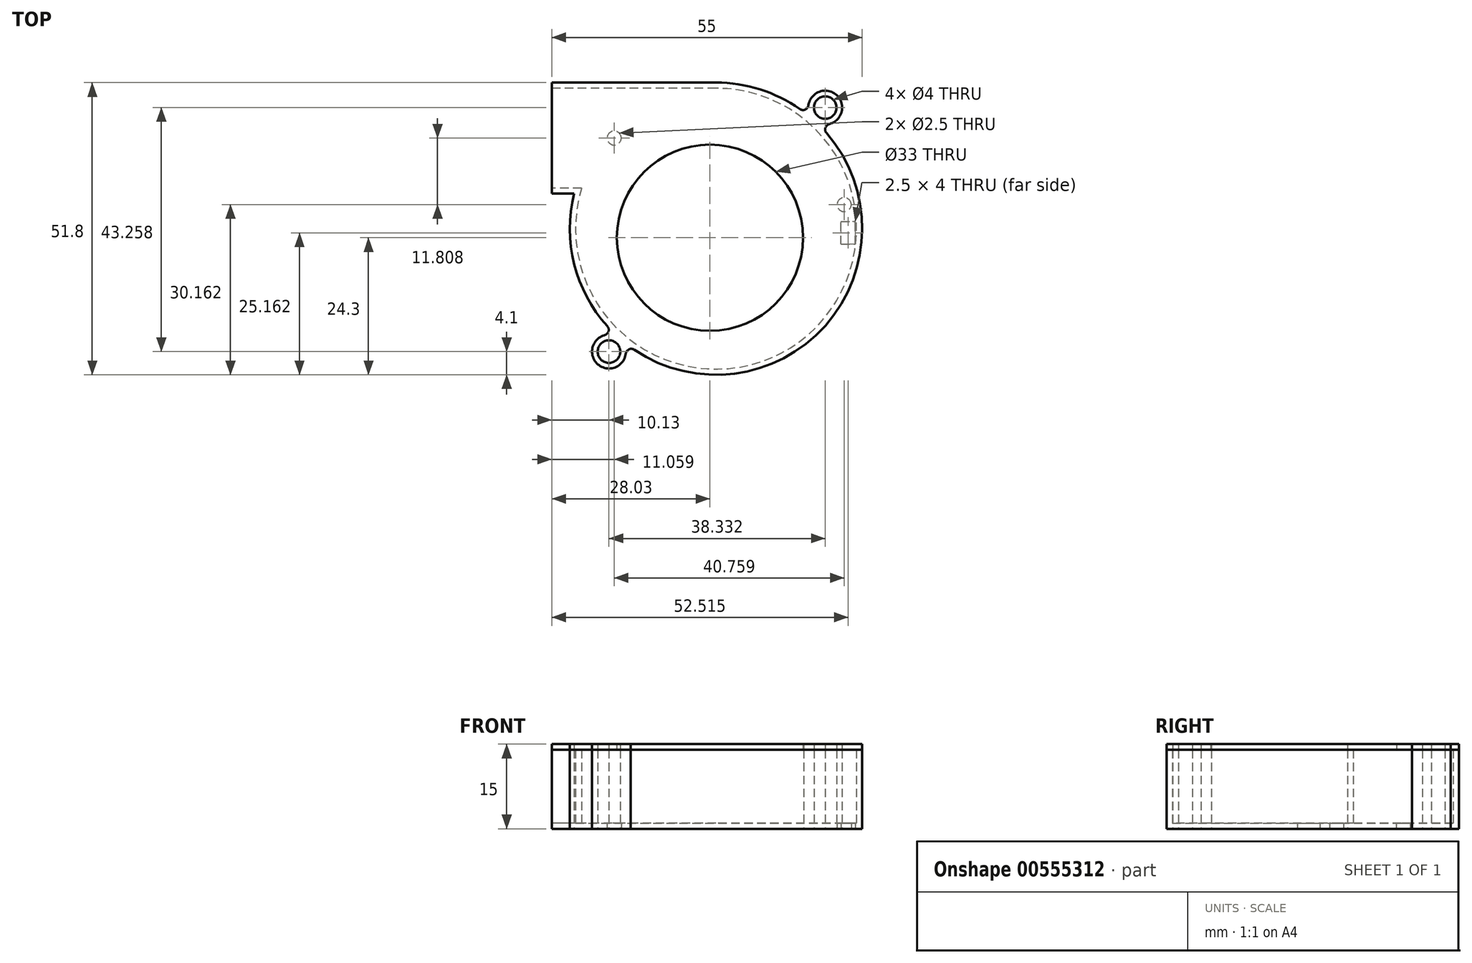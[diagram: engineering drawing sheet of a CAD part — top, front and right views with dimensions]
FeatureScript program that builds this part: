
annotation { "Feature Type Name" : "Feature", "Feature Type Description" : "" }
export const myFeature = defineFeature(function(context is Context, id is Id, definition is map)
    precondition{}
    {
        {
            var Q0;
            Q0=qCreatedBy(makeId("Top.planeOp"),FACE);
            var sketch = newSketch(context, id + "F0", { "sketchPlane" : qUnion([Q0])});
            skCircle(sketch, "E0", {"center": v(0, 0) * mm, "radius": 16.5 * mm});
            skCircle(sketch, "E1", {"center": v(1.07, 1.6) * mm, "radius": 25.9 * mm});
            skLineSegment(sketch, "E2.bottom", {"start": v(26.97, 27.5) * mm, "end": v(-24.83, 27.5) * mm, "construction": true});
            skLineSegment(sketch, "E2.top", {"start": v(26.97, -24.3) * mm, "end": v(-24.83, -24.3) * mm, "construction": true});
            skLineSegment(sketch, "E2.left", {"start": v(26.97, 27.5) * mm, "end": v(26.97, -24.3) * mm, "construction": true});
            skLineSegment(sketch, "E2.right", {"start": v(-24.83, 27.5) * mm, "end": v(-24.83, -24.3) * mm, "construction": true});
            skLineSegment(sketch, "E3", {"start": v(1.07, 27.5) * mm, "end": v(-28.03, 27.5) * mm});
            skPoint(sketch, "E3.startSnap0", {"position": v(1.07, 27.5) * mm});
            skLineSegment(sketch, "E4", {"start": v(-28.03, 27.5) * mm, "end": v(-28.03, 7.8) * mm});
            skLineSegment(sketch, "E5", {"start": v(-28.03, 7.8) * mm, "end": v(-24.07, 7.8) * mm});
            skCircle(sketch, "E6", {"center": v(20.43, 23.06) * mm, "radius": 2 * mm});
            skCircle(sketch, "E7", {"center": v(-17.9, -20.2) * mm, "radius": 2 * mm});
            skLineSegment(sketch, "E8", {"start": v(-17.9, -20.2) * mm, "end": v(24.43, 27.57) * mm, "construction": true});
            skCircle(sketch, "E9", {"center": v(20.43, 23.06) * mm, "radius": 3 * mm});
            skCircle(sketch, "E10", {"center": v(-17.9, -20.2) * mm, "radius": 3 * mm});
            skCircle(sketch, "E11", {"center": v(0, 0) * mm, "radius": 24.5 * mm, "construction": true});
            skCircle(sketch, "E12", {"center": v(-16.97, 17.67) * mm, "radius": 1.25 * mm});
            skCircle(sketch, "E13.1.0", {"center": v(23.79, 5.86) * mm, "radius": 1.25 * mm});
            skLineSegment(sketch, "E13.anchor1", {"start": v(0, 0) * mm, "end": v(-16.97, 17.67) * mm, "construction": true});
            skLineSegment(sketch, "E13.anchor2", {"start": v(0, 0) * mm, "end": v(23.79, 5.86) * mm, "construction": true});
            skLineSegment(sketch, "E14.bottom", {"start": v(23.23, -1.14) * mm, "end": v(25.73, -1.14) * mm});
            skLineSegment(sketch, "E14.top", {"start": v(23.23, 2.86) * mm, "end": v(25.73, 2.86) * mm});
            skLineSegment(sketch, "E14.left", {"start": v(23.23, -1.14) * mm, "end": v(23.23, 2.86) * mm});
            skLineSegment(sketch, "E14.right", {"start": v(25.73, -1.14) * mm, "end": v(25.73, 2.86) * mm});
            skPoint(sketch, "E14.middle", {"position": v(24.48, 0.86) * mm});
            skLineSegment(sketch, "E15", {"start": v(-15.28, -18.75) * mm, "end": v(-15.14, -18.6) * mm});
            skLineSegment(sketch, "E16", {"start": v(-16.65, -17.28) * mm, "end": v(-16.77, -17.42) * mm});
            skLineSegment(sketch, "E17", {"start": v(17.8, 21.6) * mm, "end": v(17.69, 21.47) * mm});
            skLineSegment(sketch, "E18", {"start": v(19.3, 20.28) * mm, "end": v(19.17, 20.13) * mm});
            skLineSegment(sketch, "E19", {"start": v(-28.03, 26.5) * mm, "end": v(1.07, 26.5) * mm});
            skLineSegment(sketch, "E20", {"start": v(-28.03, 8.8) * mm, "end": v(-22.76, 8.8) * mm});
            skArc(sketch, "E21", {"start": v(-22.76, 8.8) * mm, "mid": v(15.92, -18.4) * mm, "end": v(1.07, 26.5) * mm});
            skSolve(sketch);
        }
        {
            var Q0;
            {var subQ0=sQuery(id+"F0.wireOp",EDGE,"E3");Q0=makeQuery(id+"F0.imprint","IMPRINT",FACE,{"disambiguationData":[TD([[makeQuery(id+"F0.imprint","IMPRINT",EDGE,{"derivedFrom":subQ0}),1.0]])]});}
            var Q1;
            Q1=makeQuery(id+"F0.imprint","IMPRINT",FACE,{"disambiguationData":[TD([[makeQuery(id+"F0.imprint","IMPRINT",EDGE,{"derivedFrom":sQuery(id+"F0.wireOp",EDGE,"E0")}),-1.0]])]});
            var Q2;
            Q2=makeQuery(id+"F0.imprint","IMPRINT",FACE,{"disambiguationData":[TD([[makeQuery(id+"F0.imprint","IMPRINT",EDGE,{"derivedFrom":sQuery(id+"F0.wireOp",EDGE,"E0")}),1.0]])]});
            var Q3;
            Q3=makeQuery(id+"F0.imprint","IMPRINT",FACE,{"disambiguationData":[TD([[makeQuery(id+"F0.imprint","IMPRINT",EDGE,{"derivedFrom":sQuery(id+"F0.wireOp",EDGE,"E7")}),-1.0]])]});
            var Q4;
            Q4=makeQuery(id+"F0.imprint","IMPRINT",FACE,{"disambiguationData":[TD([[makeQuery(id+"F0.imprint","IMPRINT",EDGE,{"derivedFrom":sQuery(id+"F0.wireOp",EDGE,"E6")}),-1.0]])]});
            var Q5;
            {var subQ0=sQuery(id+"F0.wireOp",EDGE,"E18");Q5=makeQuery(id+"F0.imprint","IMPRINT",FACE,{"disambiguationData":[TD([[makeQuery(id+"F0.imprint","IMPRINT",EDGE,{"derivedFrom":subQ0}),-1.0]])]});}
            var Q6;
            {var subQ0=sQuery(id+"F0.wireOp",EDGE,"E17");Q6=makeQuery(id+"F0.imprint","IMPRINT",FACE,{"disambiguationData":[TD([[makeQuery(id+"F0.imprint","IMPRINT",EDGE,{"derivedFrom":subQ0}),1.0]])]});}
            var Q7;
            {var subQ0=sQuery(id+"F0.wireOp",EDGE,"E15");Q7=makeQuery(id+"F0.imprint","IMPRINT",FACE,{"disambiguationData":[TD([[makeQuery(id+"F0.imprint","IMPRINT",EDGE,{"derivedFrom":subQ0}),1.0]])]});}
            var Q8;
            {var subQ0=sQuery(id+"F0.wireOp",EDGE,"E16");Q8=makeQuery(id+"F0.imprint","IMPRINT",FACE,{"disambiguationData":[TD([[makeQuery(id+"F0.imprint","IMPRINT",EDGE,{"derivedFrom":subQ0}),1.0]])]});}
            var Q9;
            {var subQ16=sQuery(id+"F0.wireOp",EDGE,"E21");Q9=makeQuery(id+"F0.imprint","IMPRINT",FACE,{"disambiguationData":[TD([[makeQuery(id+"F0.imprint","IMPRINT",EDGE,{"derivedFrom":subQ16}),-1.0]])]});}
            var Q10;
            {var subQ0=sQuery(id+"F0.wireOp",EDGE,"E20");var subQ1=sQuery(id+"F0.wireOp",EDGE,"E1");var subQ2=makeQuery(id+"F0.imprint","INTERSECT",VERTEX,{"derivedFrom":[subQ1,subQ0]});Q10=makeQuery(id+"F0.imprint","IMPRINT",FACE,{"disambiguationData":[TD([[makeQuery(id+"F0.imprint","IMPRINT",EDGE,{"disambiguationData":[TD([[subQ2,1.0]])],"derivedFrom":subQ1}),-1.0]])]});}
            var Q11;
            {var subQ0=sQuery(id+"F0.wireOp",EDGE,"E5");Q11=makeQuery(id+"F0.imprint","IMPRINT",FACE,{"disambiguationData":[TD([[makeQuery(id+"F0.imprint","IMPRINT",EDGE,{"derivedFrom":subQ0}),1.0]])]});}
            var Q12;
            {var subQ0=sQuery(id+"F0.wireOp",EDGE,"E5");Q12=makeQuery(id+"F0.imprint","IMPRINT",FACE,{"disambiguationData":[TD([[makeQuery(id+"F0.imprint","IMPRINT",EDGE,{"derivedFrom":subQ0}),-1.0]])]});}
            extrude(context, id + "F1", {"entities" : qUnion([Q0, Q1, Q2, Q3, Q4, Q5, Q6, Q7, Q8, Q9, Q10, Q11, Q12]), "depth" : 1 * mm, "offsetDistance" : 25 * mm});
        }
        {
            var Q0;
            Q0=makeQuery(id+"F0.imprint","IMPRINT",FACE,{"disambiguationData":[TD([[makeQuery(id+"F0.imprint","IMPRINT",EDGE,{"derivedFrom":sQuery(id+"F0.wireOp",EDGE,"E7")}),-1.0]])]});
            var Q1;
            {var subQ0=sQuery(id+"F0.wireOp",EDGE,"E15");Q1=makeQuery(id+"F0.imprint","IMPRINT",FACE,{"disambiguationData":[TD([[makeQuery(id+"F0.imprint","IMPRINT",EDGE,{"derivedFrom":subQ0}),1.0]])]});}
            var Q2;
            {var subQ0=sQuery(id+"F0.wireOp",EDGE,"E16");Q2=makeQuery(id+"F0.imprint","IMPRINT",FACE,{"disambiguationData":[TD([[makeQuery(id+"F0.imprint","IMPRINT",EDGE,{"derivedFrom":subQ0}),1.0]])]});}
            var Q3;
            {var subQ16=sQuery(id+"F0.wireOp",EDGE,"E21");Q3=makeQuery(id+"F0.imprint","IMPRINT",FACE,{"disambiguationData":[TD([[makeQuery(id+"F0.imprint","IMPRINT",EDGE,{"derivedFrom":subQ16}),-1.0]])]});}
            var Q4;
            {var subQ0=sQuery(id+"F0.wireOp",EDGE,"E5");Q4=makeQuery(id+"F0.imprint","IMPRINT",FACE,{"disambiguationData":[TD([[makeQuery(id+"F0.imprint","IMPRINT",EDGE,{"derivedFrom":subQ0}),-1.0]])]});}
            var Q5;
            {var subQ0=sQuery(id+"F0.wireOp",EDGE,"E5");Q5=makeQuery(id+"F0.imprint","IMPRINT",FACE,{"disambiguationData":[TD([[makeQuery(id+"F0.imprint","IMPRINT",EDGE,{"derivedFrom":subQ0}),1.0]])]});}
            var Q6;
            {var subQ0=sQuery(id+"F0.wireOp",EDGE,"E3");Q6=makeQuery(id+"F0.imprint","IMPRINT",FACE,{"disambiguationData":[TD([[makeQuery(id+"F0.imprint","IMPRINT",EDGE,{"derivedFrom":subQ0}),1.0]])]});}
            var Q7;
            Q7=makeQuery(id+"F0.imprint","IMPRINT",FACE,{"disambiguationData":[TD([[makeQuery(id+"F0.imprint","IMPRINT",EDGE,{"derivedFrom":sQuery(id+"F0.wireOp",EDGE,"E6")}),-1.0]])]});
            var Q8;
            {var subQ0=sQuery(id+"F0.wireOp",EDGE,"E18");Q8=makeQuery(id+"F0.imprint","IMPRINT",FACE,{"disambiguationData":[TD([[makeQuery(id+"F0.imprint","IMPRINT",EDGE,{"derivedFrom":subQ0}),-1.0]])]});}
            var Q9;
            {var subQ0=sQuery(id+"F0.wireOp",EDGE,"E17");Q9=makeQuery(id+"F0.imprint","IMPRINT",FACE,{"disambiguationData":[TD([[makeQuery(id+"F0.imprint","IMPRINT",EDGE,{"derivedFrom":subQ0}),1.0]])]});}
            extrude(context, id + "F2", {"entities" : qUnion([Q0, Q1, Q2, Q3, Q4, Q5, Q6, Q7, Q8, Q9]), "operationType" : NewBodyOperationType.ADD, "depth" : 14 * mm, "offsetDistance" : 25 * mm});
        }
        {
            var Q0;
            Q0=makeQuery(id+"F0.imprint","IMPRINT",FACE,{"disambiguationData":[TD([[makeQuery(id+"F0.imprint","IMPRINT",EDGE,{"derivedFrom":sQuery(id+"F0.wireOp",EDGE,"E7")}),-1.0]])]});
            var Q1;
            {var subQ0=sQuery(id+"F0.wireOp",EDGE,"E15");Q1=makeQuery(id+"F0.imprint","IMPRINT",FACE,{"disambiguationData":[TD([[makeQuery(id+"F0.imprint","IMPRINT",EDGE,{"derivedFrom":subQ0}),1.0]])]});}
            var Q2;
            {var subQ0=sQuery(id+"F0.wireOp",EDGE,"E16");Q2=makeQuery(id+"F0.imprint","IMPRINT",FACE,{"disambiguationData":[TD([[makeQuery(id+"F0.imprint","IMPRINT",EDGE,{"derivedFrom":subQ0}),1.0]])]});}
            var Q3;
            {var subQ9=sQuery(id+"F0.wireOp",EDGE,"E21");Q3=makeQuery(id+"F0.imprint","IMPRINT",FACE,{"disambiguationData":[TD([[makeQuery(id+"F0.imprint","IMPRINT",EDGE,{"derivedFrom":subQ9}),-1.0]])]});}
            var Q4;
            Q4=makeQuery(id+"F0.imprint","IMPRINT",FACE,{"disambiguationData":[TD([[makeQuery(id+"F0.imprint","IMPRINT",EDGE,{"derivedFrom":sQuery(id+"F0.wireOp",EDGE,"E0")}),-1.0]])]});
            var Q5;
            {var subQ0=sQuery(id+"F0.wireOp",EDGE,"E5");Q5=makeQuery(id+"F0.imprint","IMPRINT",FACE,{"disambiguationData":[TD([[makeQuery(id+"F0.imprint","IMPRINT",EDGE,{"derivedFrom":subQ0}),1.0]])]});}
            var Q6;
            {var subQ0=sQuery(id+"F0.wireOp",EDGE,"E19");var subQ1=sQuery(id+"F0.wireOp",EDGE,"E1");var subQ2=makeQuery(id+"F0.imprint","INTERSECT",VERTEX,{"derivedFrom":[subQ1,subQ0]});Q6=makeQuery(id+"F0.imprint","IMPRINT",FACE,{"disambiguationData":[TD([[makeQuery(id+"F0.imprint","IMPRINT",EDGE,{"disambiguationData":[TD([[subQ2,-1.0]])],"derivedFrom":subQ1}),-1.0]])]});}
            var Q7;
            {var subQ0=sQuery(id+"F0.wireOp",EDGE,"E3");Q7=makeQuery(id+"F0.imprint","IMPRINT",FACE,{"disambiguationData":[TD([[makeQuery(id+"F0.imprint","IMPRINT",EDGE,{"derivedFrom":subQ0}),1.0]])]});}
            var Q8;
            Q8=makeQuery(id+"F0.imprint","IMPRINT",FACE,{"disambiguationData":[TD([[makeQuery(id+"F0.imprint","IMPRINT",EDGE,{"derivedFrom":sQuery(id+"F0.wireOp",EDGE,"E6")}),-1.0]])]});
            var Q9;
            {var subQ0=sQuery(id+"F0.wireOp",EDGE,"E18");Q9=makeQuery(id+"F0.imprint","IMPRINT",FACE,{"disambiguationData":[TD([[makeQuery(id+"F0.imprint","IMPRINT",EDGE,{"derivedFrom":subQ0}),-1.0]])]});}
            var Q10;
            {var subQ0=sQuery(id+"F0.wireOp",EDGE,"E17");Q10=makeQuery(id+"F0.imprint","IMPRINT",FACE,{"disambiguationData":[TD([[makeQuery(id+"F0.imprint","IMPRINT",EDGE,{"derivedFrom":subQ0}),1.0]])]});}
            var Q11;
            Q11=makeQuery(id+"F0.imprint","IMPRINT",FACE,{"disambiguationData":[TD([[makeQuery(id+"F0.imprint","IMPRINT",EDGE,{"derivedFrom":sQuery(id+"F0.wireOp",EDGE,"E14.bottom")}),1.0]])]});
            var Q12;
            Q12=makeQuery(id+"F0.imprint","IMPRINT",FACE,{"disambiguationData":[TD([[makeQuery(id+"F0.imprint","IMPRINT",EDGE,{"derivedFrom":sQuery(id+"F0.wireOp",EDGE,"E13.1.0")}),1.0]])]});
            var Q13;
            Q13=makeQuery(id+"F0.imprint","IMPRINT",FACE,{"disambiguationData":[TD([[makeQuery(id+"F0.imprint","IMPRINT",EDGE,{"derivedFrom":sQuery(id+"F0.wireOp",EDGE,"E12")}),1.0]])]});
            extrude(context, id + "F3", {"entities" : qUnion([Q0, Q1, Q2, Q3, Q4, Q5, Q6, Q7, Q8, Q9, Q10, Q11, Q12, Q13]), "depth" : 15 * mm, "offsetDistance" : 25 * mm, "hasSecondDirection" : true, "secondDirectionOppositeDirection" : false, "secondDirectionDepth" : 14 * mm});
        }
        {
            var Q0;
            {var subQ0=sQuery(id+"F0.wireOp",EDGE,"E15");var subQ1=sQuery(id+"F0.wireOp",EDGE,"E1");Q0=makeQuery(id+"F2.boolean.opBoolean","MERGE",EDGE,{"derivedFrom":[makeQuery(id+"F1.opExtrude","SWEPT_EDGE",EDGE,{"disambiguationData":[OSD([subQ1,subQ0])]}),makeQuery(id+"F2.opExtrude","SWEPT_EDGE",EDGE,{"disambiguationData":[OSD([subQ1,subQ0])]})]});}
            var Q1;
            {var subQ0=sQuery(id+"F0.wireOp",EDGE,"E16");var subQ1=sQuery(id+"F0.wireOp",EDGE,"E1");Q1=makeQuery(id+"F2.boolean.opBoolean","MERGE",EDGE,{"derivedFrom":[makeQuery(id+"F1.opExtrude","SWEPT_EDGE",EDGE,{"disambiguationData":[OSD([subQ1,subQ0])]}),makeQuery(id+"F2.opExtrude","SWEPT_EDGE",EDGE,{"disambiguationData":[OSD([subQ1,subQ0])]})]});}
            var Q2;
            {var subQ0=sQuery(id+"F0.wireOp",EDGE,"E17");var subQ1=sQuery(id+"F0.wireOp",EDGE,"E1");Q2=makeQuery(id+"F2.boolean.opBoolean","MERGE",EDGE,{"derivedFrom":[makeQuery(id+"F1.opExtrude","SWEPT_EDGE",EDGE,{"disambiguationData":[OSD([subQ1,subQ0])]}),makeQuery(id+"F2.opExtrude","SWEPT_EDGE",EDGE,{"disambiguationData":[OSD([subQ1,subQ0])]})]});}
            var Q3;
            {var subQ0=sQuery(id+"F0.wireOp",EDGE,"E18");var subQ1=sQuery(id+"F0.wireOp",EDGE,"E1");Q3=makeQuery(id+"F2.boolean.opBoolean","MERGE",EDGE,{"derivedFrom":[makeQuery(id+"F1.opExtrude","SWEPT_EDGE",EDGE,{"disambiguationData":[OSD([subQ1,subQ0])]}),makeQuery(id+"F2.opExtrude","SWEPT_EDGE",EDGE,{"disambiguationData":[OSD([subQ1,subQ0])]})]});}
            var Q4;
            Q4=makeQuery(id+"F3.opExtrude","SWEPT_EDGE",EDGE,{"disambiguationData":[OSD([sQuery(id+"F0.wireOp",EDGE,"E1"),sQuery(id+"F0.wireOp",EDGE,"E15")])]});
            var Q5;
            Q5=makeQuery(id+"F3.opExtrude","SWEPT_EDGE",EDGE,{"disambiguationData":[OSD([sQuery(id+"F0.wireOp",EDGE,"E1"),sQuery(id+"F0.wireOp",EDGE,"E16")])]});
            var Q6;
            Q6=makeQuery(id+"F3.opExtrude","SWEPT_EDGE",EDGE,{"disambiguationData":[OSD([sQuery(id+"F0.wireOp",EDGE,"E1"),sQuery(id+"F0.wireOp",EDGE,"E18")])]});
            var Q7;
            Q7=makeQuery(id+"F3.opExtrude","SWEPT_EDGE",EDGE,{"disambiguationData":[OSD([sQuery(id+"F0.wireOp",EDGE,"E1"),sQuery(id+"F0.wireOp",EDGE,"E17")])]});
            chamfer(context, id + "F4", {"entities" : qUnion([Q0, Q1, Q2, Q3, Q4, Q5, Q6, Q7]), "width" : 2 * mm, "tangentPropagation" : true});
        }
        {
            var Q0;
            {var subQ0=sQuery(id+"F0.wireOp",EDGE,"E1");var subQ1=sQuery(id+"F0.wireOp",EDGE,"E17");var subQ2=makeQuery(id+"F0.imprint","IMPRINT",EDGE,{"disambiguationData":[TD([[makeQuery(id+"F0.imprint","INTERSECT",VERTEX,{"derivedFrom":[subQ0,sQuery(id+"F0.wireOp",EDGE,"E3")]}),1.0]])],"derivedFrom":subQ0});Q0=makeQuery(id+"F4.opChamfer","BLEND_EDGE",EDGE,{"blendedFrom":[makeQuery(id+"F2.boolean.opBoolean","MERGE",EDGE,{"derivedFrom":[makeQuery(id+"F1.opExtrude","SWEPT_EDGE",EDGE,{"disambiguationData":[OSD([subQ0,subQ1])]}),makeQuery(id+"F2.opExtrude","SWEPT_EDGE",EDGE,{"disambiguationData":[OSD([subQ0,subQ1])]})]}),makeQuery(id+"F2.boolean.opBoolean","MERGE",FACE,{"derivedFrom":[makeQuery(id+"F1.opExtrude","SWEPT_FACE",FACE,{"disambiguationData":[OSD([subQ0]),TDD([subQ2])]}),makeQuery(id+"F2.opExtrude","SWEPT_FACE",FACE,{"disambiguationData":[OSD([subQ0]),TDD([subQ2])]})]})],"blendedInto":[makeQuery(id+"F2.boolean.opBoolean","MERGE",FACE,{"derivedFrom":[makeQuery(id+"F1.opExtrude","SWEPT_FACE",FACE,{"disambiguationData":[OSD([subQ0]),TDD([subQ2])]}),makeQuery(id+"F2.opExtrude","SWEPT_FACE",FACE,{"disambiguationData":[OSD([subQ0]),TDD([subQ2])]})]})]});}
            var Q1;
            {var subQ0=sQuery(id+"F0.wireOp",EDGE,"E9");var subQ1=sQuery(id+"F0.wireOp",EDGE,"E17");var subQ2=sQuery(id+"F0.wireOp",EDGE,"E1");Q1=makeQuery(id+"F4.opChamfer","BLEND_EDGE",EDGE,{"blendedFrom":[makeQuery(id+"F2.boolean.opBoolean","MERGE",EDGE,{"derivedFrom":[makeQuery(id+"F1.opExtrude","SWEPT_EDGE",EDGE,{"disambiguationData":[OSD([subQ2,subQ1])]}),makeQuery(id+"F2.opExtrude","SWEPT_EDGE",EDGE,{"disambiguationData":[OSD([subQ2,subQ1])]})]}),makeQuery(id+"F2.boolean.opBoolean","MERGE",FACE,{"derivedFrom":[makeQuery(id+"F1.opExtrude","SWEPT_FACE",FACE,{"disambiguationData":[OSD([subQ0])]}),makeQuery(id+"F2.opExtrude","SWEPT_FACE",FACE,{"disambiguationData":[OSD([subQ0])]})]})],"blendedInto":[makeQuery(id+"F2.boolean.opBoolean","MERGE",FACE,{"derivedFrom":[makeQuery(id+"F1.opExtrude","SWEPT_FACE",FACE,{"disambiguationData":[OSD([subQ0])]}),makeQuery(id+"F2.opExtrude","SWEPT_FACE",FACE,{"disambiguationData":[OSD([subQ0])]})]})]});}
            var Q2;
            {var subQ0=sQuery(id+"F0.wireOp",EDGE,"E1");var subQ1=sQuery(id+"F0.wireOp",EDGE,"E18");var subQ2=makeQuery(id+"F0.imprint","IMPRINT",EDGE,{"disambiguationData":[TD([[makeQuery(id+"F0.imprint","INTERSECT",VERTEX,{"derivedFrom":[subQ0,sQuery(id+"F0.wireOp",EDGE,"E15")]}),-1.0]])],"derivedFrom":subQ0});Q2=makeQuery(id+"F4.opChamfer","BLEND_EDGE",EDGE,{"blendedFrom":[makeQuery(id+"F2.boolean.opBoolean","MERGE",EDGE,{"derivedFrom":[makeQuery(id+"F1.opExtrude","SWEPT_EDGE",EDGE,{"disambiguationData":[OSD([subQ0,subQ1])]}),makeQuery(id+"F2.opExtrude","SWEPT_EDGE",EDGE,{"disambiguationData":[OSD([subQ0,subQ1])]})]}),makeQuery(id+"F2.boolean.opBoolean","MERGE",FACE,{"derivedFrom":[makeQuery(id+"F1.opExtrude","SWEPT_FACE",FACE,{"disambiguationData":[OSD([subQ0]),TDD([subQ2])]}),makeQuery(id+"F2.opExtrude","SWEPT_FACE",FACE,{"disambiguationData":[OSD([subQ0]),TDD([subQ2])]})]})],"blendedInto":[makeQuery(id+"F2.boolean.opBoolean","MERGE",FACE,{"derivedFrom":[makeQuery(id+"F1.opExtrude","SWEPT_FACE",FACE,{"disambiguationData":[OSD([subQ0]),TDD([subQ2])]}),makeQuery(id+"F2.opExtrude","SWEPT_FACE",FACE,{"disambiguationData":[OSD([subQ0]),TDD([subQ2])]})]})]});}
            var Q3;
            {var subQ0=sQuery(id+"F0.wireOp",EDGE,"E9");var subQ1=sQuery(id+"F0.wireOp",EDGE,"E18");var subQ2=sQuery(id+"F0.wireOp",EDGE,"E1");Q3=makeQuery(id+"F4.opChamfer","BLEND_EDGE",EDGE,{"blendedFrom":[makeQuery(id+"F2.boolean.opBoolean","MERGE",EDGE,{"derivedFrom":[makeQuery(id+"F1.opExtrude","SWEPT_EDGE",EDGE,{"disambiguationData":[OSD([subQ2,subQ1])]}),makeQuery(id+"F2.opExtrude","SWEPT_EDGE",EDGE,{"disambiguationData":[OSD([subQ2,subQ1])]})]}),makeQuery(id+"F2.boolean.opBoolean","MERGE",FACE,{"derivedFrom":[makeQuery(id+"F1.opExtrude","SWEPT_FACE",FACE,{"disambiguationData":[OSD([subQ0])]}),makeQuery(id+"F2.opExtrude","SWEPT_FACE",FACE,{"disambiguationData":[OSD([subQ0])]})]})],"blendedInto":[makeQuery(id+"F2.boolean.opBoolean","MERGE",FACE,{"derivedFrom":[makeQuery(id+"F1.opExtrude","SWEPT_FACE",FACE,{"disambiguationData":[OSD([subQ0])]}),makeQuery(id+"F2.opExtrude","SWEPT_FACE",FACE,{"disambiguationData":[OSD([subQ0])]})]})]});}
            var Q4;
            {var subQ0=sQuery(id+"F0.wireOp",EDGE,"E1");var subQ1=sQuery(id+"F0.wireOp",EDGE,"E18");Q4=makeQuery(id+"F4.opChamfer","BLEND_EDGE",EDGE,{"blendedFrom":[makeQuery(id+"F3.opExtrude","SWEPT_EDGE",EDGE,{"disambiguationData":[OSD([subQ0,subQ1])]}),makeQuery(id+"F3.opExtrude","SWEPT_FACE",FACE,{"disambiguationData":[OSD([subQ0]),TDD([makeQuery(id+"F0.imprint","IMPRINT",EDGE,{"disambiguationData":[TD([[makeQuery(id+"F0.imprint","INTERSECT",VERTEX,{"derivedFrom":[subQ0,sQuery(id+"F0.wireOp",EDGE,"E15")]}),-1.0]])],"derivedFrom":subQ0})])]})],"blendedInto":[makeQuery(id+"F3.opExtrude","SWEPT_FACE",FACE,{"disambiguationData":[OSD([subQ0]),TDD([makeQuery(id+"F0.imprint","IMPRINT",EDGE,{"disambiguationData":[TD([[makeQuery(id+"F0.imprint","INTERSECT",VERTEX,{"derivedFrom":[subQ0,sQuery(id+"F0.wireOp",EDGE,"E15")]}),-1.0]])],"derivedFrom":subQ0})])]})]});}
            var Q5;
            Q5=makeQuery(id+"F4.opChamfer","BLEND_EDGE",EDGE,{"blendedFrom":[makeQuery(id+"F3.opExtrude","SWEPT_EDGE",EDGE,{"disambiguationData":[OSD([sQuery(id+"F0.wireOp",EDGE,"E1"),sQuery(id+"F0.wireOp",EDGE,"E18")])]}),makeQuery(id+"F3.opExtrude","SWEPT_FACE",FACE,{"disambiguationData":[OSD([sQuery(id+"F0.wireOp",EDGE,"E9")])]})],"blendedInto":[makeQuery(id+"F3.opExtrude","SWEPT_FACE",FACE,{"disambiguationData":[OSD([sQuery(id+"F0.wireOp",EDGE,"E9")])]})]});
            var Q6;
            Q6=makeQuery(id+"F4.opChamfer","BLEND_EDGE",EDGE,{"blendedFrom":[makeQuery(id+"F3.opExtrude","SWEPT_EDGE",EDGE,{"disambiguationData":[OSD([sQuery(id+"F0.wireOp",EDGE,"E1"),sQuery(id+"F0.wireOp",EDGE,"E17")])]}),makeQuery(id+"F3.opExtrude","SWEPT_FACE",FACE,{"disambiguationData":[OSD([sQuery(id+"F0.wireOp",EDGE,"E9")])]})],"blendedInto":[makeQuery(id+"F3.opExtrude","SWEPT_FACE",FACE,{"disambiguationData":[OSD([sQuery(id+"F0.wireOp",EDGE,"E9")])]})]});
            var Q7;
            {var subQ0=sQuery(id+"F0.wireOp",EDGE,"E1");var subQ1=sQuery(id+"F0.wireOp",EDGE,"E17");Q7=makeQuery(id+"F4.opChamfer","BLEND_EDGE",EDGE,{"blendedFrom":[makeQuery(id+"F3.opExtrude","SWEPT_EDGE",EDGE,{"disambiguationData":[OSD([subQ0,subQ1])]}),makeQuery(id+"F3.opExtrude","SWEPT_FACE",FACE,{"disambiguationData":[OSD([subQ0]),TDD([makeQuery(id+"F0.imprint","IMPRINT",EDGE,{"disambiguationData":[TD([[makeQuery(id+"F0.imprint","INTERSECT",VERTEX,{"derivedFrom":[subQ0,sQuery(id+"F0.wireOp",EDGE,"E3")]}),1.0]])],"derivedFrom":subQ0})])]})],"blendedInto":[makeQuery(id+"F3.opExtrude","SWEPT_FACE",FACE,{"disambiguationData":[OSD([subQ0]),TDD([makeQuery(id+"F0.imprint","IMPRINT",EDGE,{"disambiguationData":[TD([[makeQuery(id+"F0.imprint","INTERSECT",VERTEX,{"derivedFrom":[subQ0,sQuery(id+"F0.wireOp",EDGE,"E3")]}),1.0]])],"derivedFrom":subQ0})])]})]});}
            var Q8;
            {var subQ0=sQuery(id+"F0.wireOp",EDGE,"E15");var subQ1=sQuery(id+"F0.wireOp",EDGE,"E1");var subQ2=makeQuery(id+"F0.imprint","IMPRINT",EDGE,{"disambiguationData":[TD([[makeQuery(id+"F0.imprint","INTERSECT",VERTEX,{"derivedFrom":[subQ1,subQ0]}),-1.0]])],"derivedFrom":subQ1});Q8=makeQuery(id+"F4.opChamfer","BLEND_EDGE",EDGE,{"blendedFrom":[makeQuery(id+"F2.boolean.opBoolean","MERGE",EDGE,{"derivedFrom":[makeQuery(id+"F1.opExtrude","SWEPT_EDGE",EDGE,{"disambiguationData":[OSD([subQ1,subQ0])]}),makeQuery(id+"F2.opExtrude","SWEPT_EDGE",EDGE,{"disambiguationData":[OSD([subQ1,subQ0])]})]}),makeQuery(id+"F2.boolean.opBoolean","MERGE",FACE,{"derivedFrom":[makeQuery(id+"F1.opExtrude","SWEPT_FACE",FACE,{"disambiguationData":[OSD([subQ1]),TDD([subQ2])]}),makeQuery(id+"F2.opExtrude","SWEPT_FACE",FACE,{"disambiguationData":[OSD([subQ1]),TDD([subQ2])]})]})],"blendedInto":[makeQuery(id+"F2.boolean.opBoolean","MERGE",FACE,{"derivedFrom":[makeQuery(id+"F1.opExtrude","SWEPT_FACE",FACE,{"disambiguationData":[OSD([subQ1]),TDD([subQ2])]}),makeQuery(id+"F2.opExtrude","SWEPT_FACE",FACE,{"disambiguationData":[OSD([subQ1]),TDD([subQ2])]})]})]});}
            var Q9;
            {var subQ0=sQuery(id+"F0.wireOp",EDGE,"E10");var subQ1=sQuery(id+"F0.wireOp",EDGE,"E15");var subQ2=sQuery(id+"F0.wireOp",EDGE,"E1");Q9=makeQuery(id+"F4.opChamfer","BLEND_EDGE",EDGE,{"blendedFrom":[makeQuery(id+"F2.boolean.opBoolean","MERGE",EDGE,{"derivedFrom":[makeQuery(id+"F1.opExtrude","SWEPT_EDGE",EDGE,{"disambiguationData":[OSD([subQ2,subQ1])]}),makeQuery(id+"F2.opExtrude","SWEPT_EDGE",EDGE,{"disambiguationData":[OSD([subQ2,subQ1])]})]}),makeQuery(id+"F2.boolean.opBoolean","MERGE",FACE,{"derivedFrom":[makeQuery(id+"F1.opExtrude","SWEPT_FACE",FACE,{"disambiguationData":[OSD([subQ0])]}),makeQuery(id+"F2.opExtrude","SWEPT_FACE",FACE,{"disambiguationData":[OSD([subQ0])]})]})],"blendedInto":[makeQuery(id+"F2.boolean.opBoolean","MERGE",FACE,{"derivedFrom":[makeQuery(id+"F1.opExtrude","SWEPT_FACE",FACE,{"disambiguationData":[OSD([subQ0])]}),makeQuery(id+"F2.opExtrude","SWEPT_FACE",FACE,{"disambiguationData":[OSD([subQ0])]})]})]});}
            var Q10;
            Q10=makeQuery(id+"F4.opChamfer","BLEND_EDGE",EDGE,{"blendedFrom":[makeQuery(id+"F3.opExtrude","SWEPT_EDGE",EDGE,{"disambiguationData":[OSD([sQuery(id+"F0.wireOp",EDGE,"E1"),sQuery(id+"F0.wireOp",EDGE,"E15")])]}),makeQuery(id+"F3.opExtrude","SWEPT_FACE",FACE,{"disambiguationData":[OSD([sQuery(id+"F0.wireOp",EDGE,"E10")])]})],"blendedInto":[makeQuery(id+"F3.opExtrude","SWEPT_FACE",FACE,{"disambiguationData":[OSD([sQuery(id+"F0.wireOp",EDGE,"E10")])]})]});
            var Q11;
            {var subQ0=sQuery(id+"F0.wireOp",EDGE,"E15");var subQ1=sQuery(id+"F0.wireOp",EDGE,"E1");Q11=makeQuery(id+"F4.opChamfer","BLEND_EDGE",EDGE,{"blendedFrom":[makeQuery(id+"F3.opExtrude","SWEPT_EDGE",EDGE,{"disambiguationData":[OSD([subQ1,subQ0])]}),makeQuery(id+"F3.opExtrude","SWEPT_FACE",FACE,{"disambiguationData":[OSD([subQ1]),TDD([makeQuery(id+"F0.imprint","IMPRINT",EDGE,{"disambiguationData":[TD([[makeQuery(id+"F0.imprint","INTERSECT",VERTEX,{"derivedFrom":[subQ1,subQ0]}),-1.0]])],"derivedFrom":subQ1})])]})],"blendedInto":[makeQuery(id+"F3.opExtrude","SWEPT_FACE",FACE,{"disambiguationData":[OSD([subQ1]),TDD([makeQuery(id+"F0.imprint","IMPRINT",EDGE,{"disambiguationData":[TD([[makeQuery(id+"F0.imprint","INTERSECT",VERTEX,{"derivedFrom":[subQ1,subQ0]}),-1.0]])],"derivedFrom":subQ1})])]})]});}
            var Q12;
            {var subQ0=sQuery(id+"F0.wireOp",EDGE,"E1");var subQ1=sQuery(id+"F0.wireOp",EDGE,"E16");Q12=makeQuery(id+"F4.opChamfer","BLEND_EDGE",EDGE,{"blendedFrom":[makeQuery(id+"F3.opExtrude","SWEPT_EDGE",EDGE,{"disambiguationData":[OSD([subQ0,subQ1])]}),makeQuery(id+"F3.opExtrude","SWEPT_FACE",FACE,{"disambiguationData":[OSD([subQ0]),TDD([makeQuery(id+"F0.imprint","IMPRINT",EDGE,{"disambiguationData":[TD([[makeQuery(id+"F0.imprint","INTERSECT",VERTEX,{"derivedFrom":[subQ0,sQuery(id+"F0.wireOp",EDGE,"E5")]}),-1.0]])],"derivedFrom":subQ0})])]})],"blendedInto":[makeQuery(id+"F3.opExtrude","SWEPT_FACE",FACE,{"disambiguationData":[OSD([subQ0]),TDD([makeQuery(id+"F0.imprint","IMPRINT",EDGE,{"disambiguationData":[TD([[makeQuery(id+"F0.imprint","INTERSECT",VERTEX,{"derivedFrom":[subQ0,sQuery(id+"F0.wireOp",EDGE,"E5")]}),-1.0]])],"derivedFrom":subQ0})])]})]});}
            var Q13;
            Q13=makeQuery(id+"F4.opChamfer","BLEND_EDGE",EDGE,{"blendedFrom":[makeQuery(id+"F3.opExtrude","SWEPT_EDGE",EDGE,{"disambiguationData":[OSD([sQuery(id+"F0.wireOp",EDGE,"E1"),sQuery(id+"F0.wireOp",EDGE,"E16")])]}),makeQuery(id+"F3.opExtrude","SWEPT_FACE",FACE,{"disambiguationData":[OSD([sQuery(id+"F0.wireOp",EDGE,"E10")])]})],"blendedInto":[makeQuery(id+"F3.opExtrude","SWEPT_FACE",FACE,{"disambiguationData":[OSD([sQuery(id+"F0.wireOp",EDGE,"E10")])]})]});
            var Q14;
            {var subQ0=sQuery(id+"F0.wireOp",EDGE,"E1");var subQ1=sQuery(id+"F0.wireOp",EDGE,"E16");var subQ2=makeQuery(id+"F0.imprint","IMPRINT",EDGE,{"disambiguationData":[TD([[makeQuery(id+"F0.imprint","INTERSECT",VERTEX,{"derivedFrom":[subQ0,sQuery(id+"F0.wireOp",EDGE,"E5")]}),-1.0]])],"derivedFrom":subQ0});Q14=makeQuery(id+"F4.opChamfer","BLEND_EDGE",EDGE,{"blendedFrom":[makeQuery(id+"F2.boolean.opBoolean","MERGE",EDGE,{"derivedFrom":[makeQuery(id+"F1.opExtrude","SWEPT_EDGE",EDGE,{"disambiguationData":[OSD([subQ0,subQ1])]}),makeQuery(id+"F2.opExtrude","SWEPT_EDGE",EDGE,{"disambiguationData":[OSD([subQ0,subQ1])]})]}),makeQuery(id+"F2.boolean.opBoolean","MERGE",FACE,{"derivedFrom":[makeQuery(id+"F1.opExtrude","SWEPT_FACE",FACE,{"disambiguationData":[OSD([subQ0]),TDD([subQ2])]}),makeQuery(id+"F2.opExtrude","SWEPT_FACE",FACE,{"disambiguationData":[OSD([subQ0]),TDD([subQ2])]})]})],"blendedInto":[makeQuery(id+"F2.boolean.opBoolean","MERGE",FACE,{"derivedFrom":[makeQuery(id+"F1.opExtrude","SWEPT_FACE",FACE,{"disambiguationData":[OSD([subQ0]),TDD([subQ2])]}),makeQuery(id+"F2.opExtrude","SWEPT_FACE",FACE,{"disambiguationData":[OSD([subQ0]),TDD([subQ2])]})]})]});}
            var Q15;
            {var subQ0=sQuery(id+"F0.wireOp",EDGE,"E10");var subQ1=sQuery(id+"F0.wireOp",EDGE,"E16");var subQ2=sQuery(id+"F0.wireOp",EDGE,"E1");Q15=makeQuery(id+"F4.opChamfer","BLEND_EDGE",EDGE,{"blendedFrom":[makeQuery(id+"F2.boolean.opBoolean","MERGE",EDGE,{"derivedFrom":[makeQuery(id+"F1.opExtrude","SWEPT_EDGE",EDGE,{"disambiguationData":[OSD([subQ2,subQ1])]}),makeQuery(id+"F2.opExtrude","SWEPT_EDGE",EDGE,{"disambiguationData":[OSD([subQ2,subQ1])]})]}),makeQuery(id+"F2.boolean.opBoolean","MERGE",FACE,{"derivedFrom":[makeQuery(id+"F1.opExtrude","SWEPT_FACE",FACE,{"disambiguationData":[OSD([subQ0])]}),makeQuery(id+"F2.opExtrude","SWEPT_FACE",FACE,{"disambiguationData":[OSD([subQ0])]})]})],"blendedInto":[makeQuery(id+"F2.boolean.opBoolean","MERGE",FACE,{"derivedFrom":[makeQuery(id+"F1.opExtrude","SWEPT_FACE",FACE,{"disambiguationData":[OSD([subQ0])]}),makeQuery(id+"F2.opExtrude","SWEPT_FACE",FACE,{"disambiguationData":[OSD([subQ0])]})]})]});}
            fillet(context, id + "F5", {"entities" : qUnion([Q0, Q1, Q2, Q3, Q4, Q5, Q6, Q7, Q8, Q9, Q10, Q11, Q12, Q13, Q14, Q15]), "tangentPropagation" : true, "radius" : 1.1 * mm, "defaultsChanged" : true, "vertexSettings" : [], "allowEdgeOverflow" : false});
        }
    });
